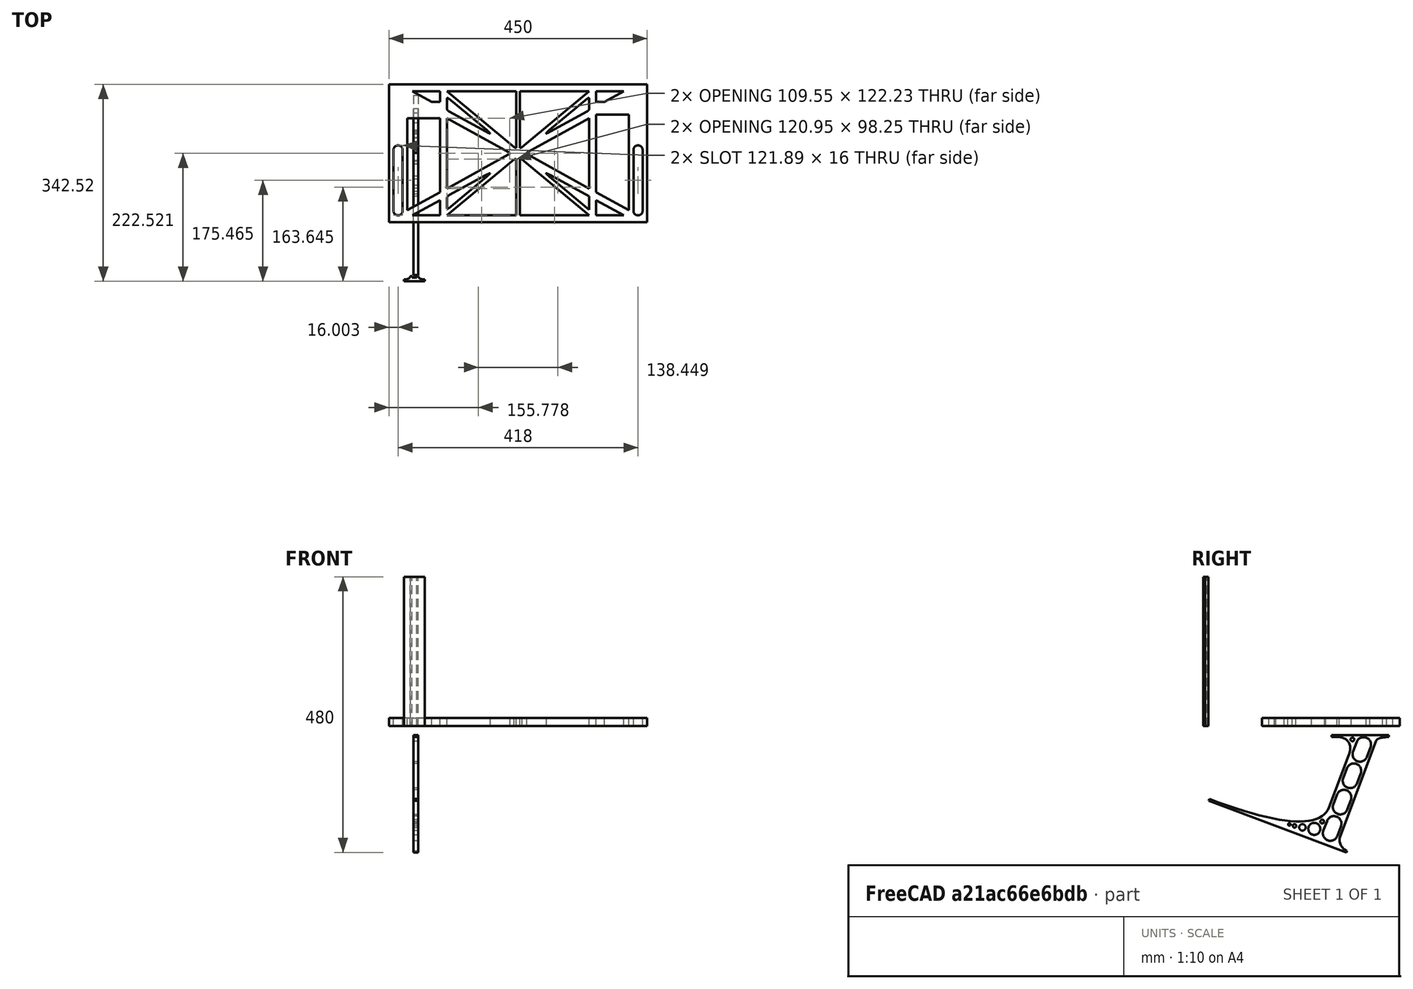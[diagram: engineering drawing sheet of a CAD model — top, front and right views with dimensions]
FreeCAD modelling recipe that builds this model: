
FCSTD DOCUMENT  (FreeCAD 0.19R0.19.2)
Label: laptopStand075
License: All rights reserved
LicenseURL: http://en.wikipedia.org/wiki/All_rights_reserved
objects: Sketcher::SketchObject×3, Part::Extrusion×3
note: 6 computed .brp shape members not serialized (recipe doc carries the construction recipe); baked Part::Feature solids carry a one-line shape summary decoded from their .brp

FEATURE [Sketcher::SketchObject] Sketch
  FullyConstrained = true
  sketch-geometry (160):
    g0: LineSegment StartX=-10.9272 StartY=-82.7794 StartZ=0 EndX=46.0728 EndY=-51.4823 EndZ=0
    g1: LineSegment StartX=366.073 StartY=-91.7794 StartZ=0 EndX=318.073 EndY=-65.424 EndZ=0
    g2: LineSegment StartX=-10.9272 StartY=77.3346 StartZ=0 EndX=-10.9272 EndY=-82.7794 EndZ=0
    g3: LineSegment StartX=375.073 StartY=-82.7794 StartZ=0 EndX=375.073 EndY=83.9235 EndZ=0
    g4: LineSegment StartX=-1.92719 StartY=-91.7794 StartZ=0 EndX=46.0728 EndY=-91.7794 EndZ=0
    g5: LineSegment StartX=318.073 StartY=124.221 StartZ=0 EndX=366.073 EndY=124.221 EndZ=0
    g6: LineSegment StartX=306.073 StartY=124.221 StartZ=0 EndX=189.124 EndY=27.0628 EndZ=0
    g7: LineSegment StartX=58.0728 StartY=-91.7794 StartZ=0 EndX=175.022 EndY=5.37834 EndZ=0
    g8: LineSegment StartX=175.022 StartY=27.0628 StartZ=0 EndX=58.0728 EndY=124.221 EndZ=0
    g9: LineSegment StartX=189.124 StartY=5.37834 StartZ=0 EndX=306.073 EndY=-91.7794 EndZ=0
    g10: LineSegment StartX=306.073 StartY=77.3346 StartZ=0 EndX=306.073 EndY=-44.8935 EndZ=0
    g11: LineSegment StartX=318.073 StartY=83.9235 StartZ=0 EndX=318.073 EndY=-51.4823 EndZ=0
    g12: LineSegment StartX=306.073 StartY=-58.8351 StartZ=0 EndX=306.073 EndY=-81.8102 EndZ=0
    g13: LineSegment StartX=318.073 StartY=-51.4823 StartZ=0 EndX=375.073 EndY=-82.7794 EndZ=0
    g14: LineSegment StartX=318.073 StartY=-65.424 StartZ=0 EndX=318.073 EndY=-91.7794 EndZ=0
    g15: LineSegment StartX=318.073 StartY=-91.7794 StartZ=0 EndX=366.073 EndY=-91.7794 EndZ=0
    g16: LineSegment StartX=58.0728 StartY=-44.8935 StartZ=0 EndX=58.0728 EndY=77.3346 EndZ=0
    g17: LineSegment StartX=46.0728 StartY=-65.424 StartZ=0 EndX=-1.92719 EndY=-91.7794 EndZ=0
    g18: LineSegment StartX=46.0728 StartY=-65.424 StartZ=0 EndX=46.0728 EndY=-91.7794 EndZ=0
    g19: LineSegment StartX=46.0728 StartY=77.3346 StartZ=0 EndX=46.0728 EndY=-51.4823 EndZ=0
    g20: LineSegment StartX=-42.9272 StartY=136.221 StartZ=0 EndX=-42.9272 EndY=-103.779 EndZ=0
    g21: LineSegment StartX=407.073 StartY=136.221 StartZ=0 EndX=407.073 EndY=-103.779 EndZ=0
    g22: LineSegment StartX=179.022 StartY=27.0628 StartZ=0 EndX=179.022 EndY=124.221 EndZ=0
    g23: LineSegment StartX=185.124 StartY=27.0628 StartZ=0 EndX=185.124 EndY=124.221 EndZ=0
    g24: ArcOfCircle CenterX=-26.9272 CenterY=22.1087 CenterZ=0 NormalX=0 NormalY=0 NormalZ=1 AngleXU=0 Radius=8 StartAngle=1e-16 EndAngle=3.14159
    g25: ArcOfCircle CenterX=-26.9272 CenterY=-83.7794 CenterZ=0 NormalX=0 NormalY=0 NormalZ=1 AngleXU=0 Radius=8 StartAngle=3.14159 EndAngle=6.28319
    g26: LineSegment StartX=-34.9272 StartY=22.1087 StartZ=0 EndX=-34.9272 EndY=-83.7794 EndZ=0
    g27: LineSegment StartX=-18.9272 StartY=22.1087 StartZ=0 EndX=-18.9272 EndY=-83.7794 EndZ=0
    g28: LineSegment StartX=185.124 StartY=-91.7794 StartZ=0 EndX=306.073 EndY=-91.7794 EndZ=0
    g29: LineSegment StartX=179.022 StartY=-91.7794 StartZ=0 EndX=58.0728 EndY=-91.7794 EndZ=0
    g30: LineSegment StartX=306.073 StartY=124.221 StartZ=0 EndX=185.124 EndY=124.221 EndZ=0
    g31: LineSegment StartX=179.022 StartY=124.221 StartZ=0 EndX=58.0728 EndY=124.221 EndZ=0
    g32: ArcOfCircle CenterX=391.073 CenterY=22.1087 CenterZ=0 NormalX=0 NormalY=0 NormalZ=1 AngleXU=0 Radius=8 StartAngle=-4.4e-15 EndAngle=3.14159
    g33: LineSegment StartX=399.073 StartY=22.1087 StartZ=0 EndX=399.073 EndY=-83.7794 EndZ=0
    g34: LineSegment StartX=383.073 StartY=22.1087 StartZ=0 EndX=383.073 EndY=-83.7794 EndZ=0
    g35: ArcOfCircle CenterX=391.073 CenterY=-83.7794 CenterZ=0 NormalX=0 NormalY=0 NormalZ=1 AngleXU=0 Radius=8 StartAngle=3.14159 EndAngle=6.28319
    g36: Circle CenterX=175.022 CenterY=27.0628 CenterZ=0 NormalX=0 NormalY=0 NormalZ=1 AngleXU=0 Radius=1
    g37: Circle CenterX=179.022 CenterY=24.8665 CenterZ=0 NormalX=0 NormalY=0 NormalZ=1 AngleXU=0 Radius=1
    g38: Circle CenterX=179.022 CenterY=27.0628 CenterZ=0 NormalX=0 NormalY=0 NormalZ=1 AngleXU=0 Radius=1
    g39: BSplineCurve PolesCount=3 KnotsCount=2 Degree=2 IsPeriodic=0
    g40: GeomPoint X=175.022 Y=27.0628 Z=0
    g41: GeomPoint X=179.022 Y=27.0628 Z=0
    g42: Circle CenterX=189.124 CenterY=27.0628 CenterZ=0 NormalX=0 NormalY=0 NormalZ=1 AngleXU=0 Radius=1
    g43: Circle CenterX=185.124 CenterY=24.8665 CenterZ=0 NormalX=0 NormalY=0 NormalZ=1 AngleXU=0 Radius=1
    g44: Circle CenterX=185.124 CenterY=27.0628 CenterZ=0 NormalX=0 NormalY=0 NormalZ=1 AngleXU=0 Radius=1
    g45: BSplineCurve PolesCount=3 KnotsCount=2 Degree=2 IsPeriodic=0
    g46: GeomPoint X=189.124 Y=27.0628 Z=0
    g47: GeomPoint X=185.124 Y=27.0628 Z=0
    g48: Circle CenterX=175.022 CenterY=5.37834 CenterZ=0 NormalX=0 NormalY=0 NormalZ=1 AngleXU=0 Radius=1
    g49: Circle CenterX=179.022 CenterY=7.57463 CenterZ=0 NormalX=0 NormalY=0 NormalZ=1 AngleXU=0 Radius=1
    g50: Circle CenterX=179.022 CenterY=5.34704 CenterZ=0 NormalX=0 NormalY=0 NormalZ=1 AngleXU=0 Radius=1
    g51: BSplineCurve PolesCount=3 KnotsCount=2 Degree=2 IsPeriodic=0
    g52: GeomPoint X=175.022 Y=5.37834 Z=0
    g53: GeomPoint X=179.022 Y=5.34704 Z=0
    g54: Circle CenterX=189.124 CenterY=5.37834 CenterZ=0 NormalX=0 NormalY=0 NormalZ=1 AngleXU=0 Radius=1
    g55: Circle CenterX=185.124 CenterY=7.57463 CenterZ=0 NormalX=0 NormalY=0 NormalZ=1 AngleXU=0 Radius=1
    g56: Circle CenterX=185.124 CenterY=5.34704 CenterZ=0 NormalX=0 NormalY=0 NormalZ=1 AngleXU=0 Radius=1
    g57: BSplineCurve PolesCount=3 KnotsCount=2 Degree=2 IsPeriodic=0
    g58: GeomPoint X=189.124 Y=5.37834 Z=0
    g59: GeomPoint X=185.124 Y=5.34704 Z=0
    g60: LineSegment StartX=179.022 StartY=5.34704 StartZ=0 EndX=179.022 EndY=-91.7794 EndZ=0
    g61: LineSegment StartX=185.124 StartY=-91.7794 StartZ=0 EndX=185.124 EndY=5.34704 EndZ=0
    g62: Circle CenterX=165.871 CenterY=18.1458 CenterZ=0 NormalX=0 NormalY=0 NormalZ=1 AngleXU=0 Radius=1
    g63: Circle CenterX=169.377 CenterY=16.2206 CenterZ=0 NormalX=0 NormalY=0 NormalZ=1 AngleXU=0 Radius=1
    g64: Circle CenterX=165.871 CenterY=14.2954 CenterZ=0 NormalX=0 NormalY=0 NormalZ=1 AngleXU=0 Radius=1
    g65: BSplineCurve PolesCount=3 KnotsCount=2 Degree=2 IsPeriodic=0
    g66: GeomPoint X=165.871 Y=18.1458 Z=0
    g67: GeomPoint X=165.871 Y=14.2954 Z=0
    g68: Circle CenterX=198.275 CenterY=18.1458 CenterZ=0 NormalX=0 NormalY=0 NormalZ=1 AngleXU=0 Radius=1
    g69: Circle CenterX=194.768 CenterY=16.2206 CenterZ=0 NormalX=0 NormalY=0 NormalZ=1 AngleXU=0 Radius=1
    g70: Circle CenterX=198.275 CenterY=14.2954 CenterZ=0 NormalX=0 NormalY=0 NormalZ=1 AngleXU=0 Radius=1
    g71: BSplineCurve PolesCount=3 KnotsCount=2 Degree=2 IsPeriodic=0
    g72: GeomPoint X=198.275 Y=18.1458 Z=0
    g73: GeomPoint X=198.275 Y=14.2954 Z=0
    g74: LineSegment StartX=165.871 StartY=18.1458 StartZ=0 EndX=58.0728 EndY=77.3346 EndZ=0
    g75: LineSegment StartX=58.0728 StartY=-44.8935 StartZ=0 EndX=165.871 EndY=14.2954 EndZ=0
    g76: LineSegment StartX=198.275 StartY=18.1458 StartZ=0 EndX=306.073 EndY=77.3346 EndZ=0
    g77: LineSegment StartX=198.275 StartY=14.2954 StartZ=0 EndX=306.073 EndY=-44.8935 EndZ=0
    g78: LineSegment StartX=407.073 StartY=-103.779 StartZ=0 EndX=-42.9272 EndY=-103.779 EndZ=0
    g79: LineSegment StartX=407.073 StartY=136.221 StartZ=0 EndX=-42.9272 EndY=136.221 EndZ=0
    g80: LineSegment StartX=46.0728 StartY=77.3346 StartZ=0 EndX=-10.9272 EndY=77.3346 EndZ=0
    g81: LineSegment StartX=46.0728 StartY=105.865 StartZ=0 EndX=31.5028 EndY=105.865 EndZ=0
    g82: LineSegment StartX=46.0728 StartY=124.221 StartZ=0 EndX=46.0728 EndY=105.865 EndZ=0
    g83: LineSegment StartX=-1.92719 StartY=124.221 StartZ=0 EndX=31.5028 EndY=105.865 EndZ=0
    g84: LineSegment StartX=46.0728 StartY=124.221 StartZ=0 EndX=-1.92719 EndY=124.221 EndZ=0
    g85: LineSegment StartX=318.073 StartY=83.9235 StartZ=0 EndX=375.073 EndY=83.9235 EndZ=0
    g86: LineSegment StartX=318.073 StartY=105.865 StartZ=0 EndX=332.643 EndY=105.865 EndZ=0
    g87: LineSegment StartX=332.643 StartY=105.865 StartZ=0 EndX=366.073 EndY=124.221 EndZ=0
    g88: LineSegment StartX=318.073 StartY=124.221 StartZ=0 EndX=318.073 EndY=105.865 EndZ=0
    g89: Circle CenterX=125.607 CenterY=54.1951 CenterZ=0 NormalX=0 NormalY=0 NormalZ=1 AngleXU=0 Radius=1
    g90: Circle CenterX=139.632 CenterY=46.4944 CenterZ=0 NormalX=0 NormalY=0 NormalZ=1 AngleXU=0 Radius=1
    g91: Circle CenterX=127.326 CenterY=56.7187 CenterZ=0 NormalX=0 NormalY=0 NormalZ=1 AngleXU=0 Radius=1
    g92: BSplineCurve PolesCount=3 KnotsCount=2 Degree=2 IsPeriodic=0
    g93: GeomPoint X=125.607 Y=54.1951 Z=0
    g94: GeomPoint X=127.326 Y=56.7187 Z=0
    g95: Circle CenterX=236.821 CenterY=56.7187 CenterZ=0 NormalX=0 NormalY=0 NormalZ=1 AngleXU=0 Radius=1
    g96: Circle CenterX=224.513 CenterY=46.4944 CenterZ=0 NormalX=0 NormalY=0 NormalZ=1 AngleXU=0 Radius=1
    g97: Circle CenterX=238.538 CenterY=54.1951 CenterZ=0 NormalX=0 NormalY=0 NormalZ=1 AngleXU=0 Radius=1
    g98: BSplineCurve PolesCount=3 KnotsCount=2 Degree=2 IsPeriodic=0
    g99: GeomPoint X=236.821 Y=56.7187 Z=0
    g100: GeomPoint X=238.538 Y=54.1951 Z=0
    g101: Circle CenterX=238.538 CenterY=-21.7539 CenterZ=0 NormalX=0 NormalY=0 NormalZ=1 AngleXU=0 Radius=1
    g102: Circle CenterX=224.513 CenterY=-14.0532 CenterZ=0 NormalX=0 NormalY=0 NormalZ=1 AngleXU=0 Radius=1
    g103: Circle CenterX=236.821 CenterY=-24.2775 CenterZ=0 NormalX=0 NormalY=0 NormalZ=1 AngleXU=0 Radius=1
    g104: BSplineCurve PolesCount=3 KnotsCount=2 Degree=2 IsPeriodic=0
    g105: GeomPoint X=238.538 Y=-21.7539 Z=0
    g106: GeomPoint X=236.821 Y=-24.2775 Z=0
    g107: LineSegment StartX=238.538 StartY=-21.7539 StartZ=0 EndX=306.073 EndY=-58.8351 EndZ=0
    g108: LineSegment StartX=236.821 StartY=-24.2775 StartZ=0 EndX=306.073 EndY=-81.8102 EndZ=0
    g109: Circle CenterX=125.607 CenterY=-21.7539 CenterZ=0 NormalX=0 NormalY=0 NormalZ=1 AngleXU=0 Radius=1
    g110: Circle CenterX=139.632 CenterY=-14.0532 CenterZ=0 NormalX=0 NormalY=0 NormalZ=1 AngleXU=0 Radius=1
    g111: Circle CenterX=127.325 CenterY=-24.2775 CenterZ=0 NormalX=0 NormalY=0 NormalZ=1 AngleXU=0 Radius=1
    g112: BSplineCurve PolesCount=3 KnotsCount=2 Degree=2 IsPeriodic=0
    g113: GeomPoint X=125.607 Y=-21.7539 Z=0
    g114: GeomPoint X=127.325 Y=-24.2775 Z=0
    g115: Circle CenterX=302.996 CenterY=111.695 CenterZ=0 NormalX=0 NormalY=0 NormalZ=1 AngleXU=0 Radius=1
    g116: Circle CenterX=306.073 CenterY=114.251 CenterZ=0 NormalX=0 NormalY=0 NormalZ=1 AngleXU=0 Radius=1
    g117: Circle CenterX=306.073 CenterY=110.251 CenterZ=0 NormalX=0 NormalY=0 NormalZ=1 AngleXU=0 Radius=1
    g118: BSplineCurve PolesCount=3 KnotsCount=2 Degree=2 IsPeriodic=0
    g119: GeomPoint X=302.996 Y=111.695 Z=0
    g120: GeomPoint X=306.073 Y=110.251 Z=0
    g121: Circle CenterX=306.073 CenterY=95.2763 CenterZ=0 NormalX=0 NormalY=0 NormalZ=1 AngleXU=0 Radius=1
    g122: Circle CenterX=306.073 CenterY=91.2763 CenterZ=0 NormalX=0 NormalY=0 NormalZ=1 AngleXU=0 Radius=1
    g123: Circle CenterX=302.567 CenterY=89.3511 CenterZ=0 NormalX=0 NormalY=0 NormalZ=1 AngleXU=0 Radius=1
    g124: BSplineCurve PolesCount=3 KnotsCount=2 Degree=2 IsPeriodic=0
    g125: GeomPoint X=306.073 Y=95.2763 Z=0
    g126: GeomPoint X=302.567 Y=89.3511 Z=0
    g127: LineSegment StartX=306.073 StartY=110.251 StartZ=0 EndX=306.073 EndY=95.2763 EndZ=0
    g128: LineSegment StartX=302.996 StartY=111.695 StartZ=0 EndX=236.821 EndY=56.7187 EndZ=0
    g129: LineSegment StartX=238.538 StartY=54.1951 StartZ=0 EndX=302.567 EndY=89.3511 EndZ=0
    g130: Circle CenterX=61.1496 CenterY=111.695 CenterZ=0 NormalX=0 NormalY=0 NormalZ=1 AngleXU=0 Radius=1
    g131: Circle CenterX=58.0728 CenterY=114.251 CenterZ=0 NormalX=0 NormalY=0 NormalZ=1 AngleXU=0 Radius=1
    g132: Circle CenterX=58.0728 CenterY=110.251 CenterZ=0 NormalX=0 NormalY=0 NormalZ=1 AngleXU=0 Radius=1
    g133: BSplineCurve PolesCount=3 KnotsCount=2 Degree=2 IsPeriodic=0
    g134: GeomPoint X=61.1496 Y=111.695 Z=0
    g135: GeomPoint X=58.0728 Y=110.251 Z=0
    g136: Circle CenterX=61.5791 CenterY=89.3511 CenterZ=0 NormalX=0 NormalY=0 NormalZ=1 AngleXU=0 Radius=1
    g137: Circle CenterX=58.0728 CenterY=91.2763 CenterZ=0 NormalX=0 NormalY=0 NormalZ=1 AngleXU=0 Radius=1
    g138: Circle CenterX=58.0728 CenterY=95.2763 CenterZ=0 NormalX=0 NormalY=0 NormalZ=1 AngleXU=0 Radius=1
    g139: BSplineCurve PolesCount=3 KnotsCount=2 Degree=2 IsPeriodic=0
    g140: GeomPoint X=61.5791 Y=89.3511 Z=0
    g141: GeomPoint X=58.0728 Y=95.2763 Z=0
    g142: LineSegment StartX=58.0728 StartY=110.251 StartZ=0 EndX=58.0728 EndY=95.2763 EndZ=0
    g143: LineSegment StartX=61.1496 StartY=111.695 StartZ=0 EndX=127.326 EndY=56.7187 EndZ=0
    g144: LineSegment StartX=125.607 StartY=54.1951 StartZ=0 EndX=61.5791 EndY=89.3511 EndZ=0
    g145: Circle CenterX=61.5791 CenterY=-56.9099 CenterZ=0 NormalX=0 NormalY=0 NormalZ=1 AngleXU=0 Radius=1
    g146: Circle CenterX=58.0728 CenterY=-58.8351 CenterZ=0 NormalX=0 NormalY=0 NormalZ=1 AngleXU=0 Radius=1
    g147: Circle CenterX=58.0728 CenterY=-62.8351 CenterZ=0 NormalX=0 NormalY=0 NormalZ=1 AngleXU=0 Radius=1
    g148: BSplineCurve PolesCount=3 KnotsCount=2 Degree=2 IsPeriodic=0
    g149: GeomPoint X=61.5791 Y=-56.9099 Z=0
    g150: GeomPoint X=58.0728 Y=-62.8351 Z=0
    g151: Circle CenterX=58.0728 CenterY=-77.8102 CenterZ=0 NormalX=0 NormalY=0 NormalZ=1 AngleXU=0 Radius=1
    g152: Circle CenterX=58.0728 CenterY=-81.8102 CenterZ=0 NormalX=0 NormalY=0 NormalZ=1 AngleXU=0 Radius=1
    g153: Circle CenterX=61.1496 CenterY=-79.2541 CenterZ=0 NormalX=0 NormalY=0 NormalZ=1 AngleXU=0 Radius=1
    g154: BSplineCurve PolesCount=3 KnotsCount=2 Degree=2 IsPeriodic=0
    g155: GeomPoint X=58.0728 Y=-77.8102 Z=0
    g156: GeomPoint X=61.1496 Y=-79.2541 Z=0
    g157: LineSegment StartX=58.0728 StartY=-62.8351 StartZ=0 EndX=58.0728 EndY=-77.8102 EndZ=0
    g158: LineSegment StartX=61.1496 StartY=-79.2541 StartZ=0 EndX=127.325 EndY=-24.2775 EndZ=0
    g159: LineSegment StartX=125.607 StartY=-21.7539 StartZ=0 EndX=61.5791 EndY=-56.9099 EndZ=0
  constraints (281):
    c: Horizontal(g4)
    c: Horizontal(g5)
    c: Tangent(g10,g12)
    c: Coincident(g11,g13)
    c: Coincident(g14,g1)
    c: Tangent(g11,g14)
    c: Coincident(g18,g17)
    c: Coincident(g0,g19)
    c: Block(g8)
    c: Block(g6)
    c: Block(g13)
    c: Block(g3)
    c: Block(g12)
    c: Block(g1)
    c: Block(g14)
    c: Block(g9)
    c: Block(g7)
    c: Block(g18)
    c: Block(g17)
    c: Block(g0)
    c: Block(g2)
    c: Block(g10)
    c: Block(g5)
    c: Block(g15)
    c: Block(g4)
    c: Vertical(g20)
    c: Vertical(g21)
    c: Block(g21)
    c: Block(g20)
    c: Vertical(g22)
    c: Vertical(g23)
    c: Block(g22)
    c: Block(g23)
    c: Tangent(g24,g27) = 1.5708
    c: Tangent(g24,g26) = -1.5708
    c: Tangent(g26,g25) = -1.5708
    c: Tangent(g27,g25) = 1.5708
    c: Vertical(g26)
    c: Equal(g24,g25)
    c: Block(g27)
    c: Block(g26)
    c: Coincident(g28,g9)
    c: Horizontal(g28)
    c: Coincident(g29,g7)
    c: Horizontal(g29)
    c: Coincident(g30,g6)
    c: Coincident(g30,g23)
    c: Horizontal(g30)
    c: Coincident(g31,g22)
    c: Coincident(g31,g8)
    c: Horizontal(g31)
    c: Tangent(g32,g33) = 1.5708
    c: Tangent(g33,g35) = 1.5708
    c: Equal(g32,g35)
    c: Coincident(g34,g32)
    c: Coincident(g34,g35)
    c: Block(g33)
    c: Block(g34)
    c: Coincident(g39,g8)
    c: Weight(g36) = 1
    c: Equal(g36,g37)
    c: Equal(g36,g38)
    c: Coincident(g39,g22)
    c: InternalAlignment(g36,g39)
    c: InternalAlignment(g37,g39)
    c: InternalAlignment(g38,g39)
    c: InternalAlignment(g40,g39)
    c: InternalAlignment(g41,g39)
    c: Coincident(g45,g6)
    c: Weight(g42) = 1
    c: Equal(g42,g43)
    c: Equal(g42,g44)
    c: Coincident(g45,g23)
    c: InternalAlignment(g42,g45)
    c: InternalAlignment(g43,g45)
    c: InternalAlignment(g44,g45)
    c: InternalAlignment(g46,g45)
    c: InternalAlignment(g47,g45)
    c: Block(g45)
    c: Block(g39)
    c: Coincident(g51,g7)
    c: Weight(g48) = 1
    c: Equal(g48,g49)
    c: Equal(g48,g50)
    c: InternalAlignment(g48,g51)
    c: InternalAlignment(g49,g51)
    c: InternalAlignment(g50,g51)
    c: InternalAlignment(g52,g51)
    c: InternalAlignment(g53,g51)
    c: Weight(g54) = 1
    c: Equal(g54,g55)
    c: Equal(g54,g56)
    c: InternalAlignment(g54,g57)
    c: InternalAlignment(g55,g57)
    c: InternalAlignment(g56,g57)
    c: InternalAlignment(g58,g57)
    c: InternalAlignment(g59,g57)
    c: Block(g57)
    c: Block(g51)
    c: Coincident(g60,g51)
    c: Coincident(g60,g29)
    c: Vertical(g60)
    c: Coincident(g61,g28)
    c: Coincident(g61,g57)
    c: Vertical(g61)
    c: Weight(g62) = 1
    c: Equal(g62,g63)
    c: Equal(g62,g64)
    c: InternalAlignment(g62,g65)
    c: InternalAlignment(g63,g65)
    c: InternalAlignment(g64,g65)
    c: InternalAlignment(g66,g65)
    c: InternalAlignment(g67,g65)
    c: Weight(g68) = 1
    c: Equal(g68,g69)
    c: Equal(g68,g70)
    c: InternalAlignment(g68,g71)
    c: InternalAlignment(g69,g71)
    c: InternalAlignment(g70,g71)
    c: InternalAlignment(g72,g71)
    c: InternalAlignment(g73,g71)
    c: Block(g65)
    c: Block(g71)
    c: Coincident(g74,g65)
    c: Coincident(g74,g16)
    c: Coincident(g75,g16)
    c: Coincident(g75,g65)
    c: Coincident(g76,g71)
    c: Coincident(g76,g10)
    c: Coincident(g77,g71)
    c: Coincident(g77,g10)
    c: Block(g16)
    c: Coincident(g78,g21)
    c: Coincident(g78,g20)
    c: Horizontal(g78)
    c: Distance(g78) = 450
    c: Coincident(g79,g21)
    c: Coincident(g79,g20)
    c: Horizontal(g79)
    c: Horizontal(g80)
    c: Coincident(g19,g80)
    c: Horizontal(g81)
    c: Vertical(g82)
    c: Block(g82)
    c: Block(g81)
    c: Block(g80)
    c: Distance(g82) = 18.3554
    c: Coincident(g84,g82)
    c: Coincident(g84,g83)
    c: Horizontal(g84)
    c: Block(g84)
    c: Block(g83)
    c: Coincident(g81,g83)
    c: Coincident(g2,g80)
    c: Coincident(g85,g11)
    c: Horizontal(g85)
    c: Horizontal(g86)
    c: Block(g85)
    c: Coincident(g87,g5)
    c: Coincident(g88,g5)
    c: Coincident(g88,g86)
    c: Vertical(g88)
    c: Block(g88)
    c: Coincident(g86,g87)
    c: Block(g87)
    c: Coincident(g3,g85)
    c: Weight(g89) = 1
    c: Equal(g89,g90)
    c: Equal(g89,g91)
    c: InternalAlignment(g89,g92)
    c: InternalAlignment(g90,g92)
    c: InternalAlignment(g91,g92)
    c: InternalAlignment(g93,g92)
    c: InternalAlignment(g94,g92)
    c: Block(g92)
    c: Weight(g95) = 1
    c: Equal(g95,g96)
    c: Equal(g95,g97)
    c: InternalAlignment(g95,g98)
    c: InternalAlignment(g96,g98)
    c: InternalAlignment(g97,g98)
    c: InternalAlignment(g99,g98)
    c: InternalAlignment(g100,g98)
    c: Block(g98)
    c: Weight(g101) = 1
    c: Equal(g101,g102)
    c: Equal(g101,g103)
    c: InternalAlignment(g101,g104)
    c: InternalAlignment(g102,g104)
    c: InternalAlignment(g103,g104)
    c: InternalAlignment(g105,g104)
    c: InternalAlignment(g106,g104)
    c: Block(g104)
    c: Coincident(g107,g104)
    c: Coincident(g107,g12)
    c: Coincident(g108,g104)
    c: Coincident(g108,g12)
    c: Weight(g109) = 1
    c: Equal(g109,g110)
    c: Equal(g109,g111)
    c: InternalAlignment(g109,g112)
    c: InternalAlignment(g110,g112)
    c: InternalAlignment(g111,g112)
    c: InternalAlignment(g113,g112)
    c: InternalAlignment(g114,g112)
    c: Block(g112)
    c: Weight(g115) = 1
    c: Equal(g115,g116)
    c: Equal(g115,g117)
    c: InternalAlignment(g115,g118)
    c: InternalAlignment(g116,g118)
    c: InternalAlignment(g117,g118)
    c: InternalAlignment(g119,g118)
    c: InternalAlignment(g120,g118)
    c: Weight(g121) = 1
    c: Equal(g121,g122)
    c: Equal(g121,g123)
    c: InternalAlignment(g121,g124)
    c: InternalAlignment(g122,g124)
    c: InternalAlignment(g123,g124)
    c: InternalAlignment(g125,g124)
    c: InternalAlignment(g126,g124)
    c: Block(g118)
    c: Block(g124)
    c: Coincident(g127,g118)
    c: Coincident(g127,g124)
    c: Vertical(g127)
    c: Coincident(g128,g118)
    c: Coincident(g128,g98)
    c: Coincident(g129,g98)
    c: Coincident(g129,g124)
    c: Weight(g130) = 1
    c: Equal(g130,g131)
    c: Equal(g130,g132)
    c: InternalAlignment(g130,g133)
    c: InternalAlignment(g131,g133)
    c: InternalAlignment(g132,g133)
    c: InternalAlignment(g134,g133)
    c: InternalAlignment(g135,g133)
    c: Weight(g136) = 1
    c: Equal(g136,g137)
    c: Equal(g136,g138)
    c: InternalAlignment(g136,g139)
    c: InternalAlignment(g137,g139)
    c: InternalAlignment(g138,g139)
    c: InternalAlignment(g140,g139)
    c: InternalAlignment(g141,g139)
    c: Block(g133)
    c: Block(g139)
    c: Coincident(g142,g133)
    c: Coincident(g142,g139)
    c: Vertical(g142)
    c: Coincident(g143,g133)
    c: Coincident(g143,g92)
    c: Coincident(g144,g92)
    c: Coincident(g144,g139)
    c: Weight(g145) = 1
    c: Equal(g145,g146)
    c: Equal(g145,g147)
    c: InternalAlignment(g145,g148)
    c: InternalAlignment(g146,g148)
    c: InternalAlignment(g147,g148)
    c: InternalAlignment(g149,g148)
    c: InternalAlignment(g150,g148)
    c: Weight(g151) = 1
    c: Equal(g151,g152)
    c: Equal(g151,g153)
    c: InternalAlignment(g151,g154)
    c: InternalAlignment(g152,g154)
    c: InternalAlignment(g153,g154)
    c: InternalAlignment(g155,g154)
    c: InternalAlignment(g156,g154)
    c: Block(g148)
    c: Block(g154)
    c: Coincident(g157,g148)
    c: Coincident(g157,g154)
    c: Vertical(g157)
    c: Coincident(g158,g154)
    c: Coincident(g158,g112)
    c: Coincident(g159,g112)
    c: Coincident(g159,g148)
FEATURE [Sketcher::SketchObject] Sketch001
  FullyConstrained = true
  MapMode = 4
  Placement = pos=(0,0,0) rot=(0.57735,0.57735,0.57735;2.0944rad)
  Support = -> [Sketch]
  sketch-geometry (46):
    g0: BSplineCurve PolesCount=3 KnotsCount=2 Degree=2 IsPeriodic=0
    g1: ArcOfCircle CenterX=73.1223 CenterY=-32.291 CenterZ=0 NormalX=0 NormalY=0 NormalZ=1 AngleXU=0 Radius=13 StartAngle=5.92268 EndAngle=9.06428
    g2: ArcOfCircle CenterX=66.7816 CenterY=-49.1439 CenterZ=0 NormalX=0 NormalY=0 NormalZ=1 AngleXU=0 Radius=13 StartAngle=2.78068 EndAngle=5.92131
    g3: ArcOfCircle CenterX=55.9263 CenterY=-78.1807 CenterZ=0 NormalX=0 NormalY=0 NormalZ=1 AngleXU=0 Radius=13 StartAngle=5.92268 EndAngle=9.06428
    g4: ArcOfCircle CenterX=49.5884 CenterY=-95.0342 CenterZ=0 NormalX=0 NormalY=0 NormalZ=1 AngleXU=0 Radius=13 StartAngle=2.78068 EndAngle=5.92131
    g5: ArcOfCircle CenterX=38.7206 CenterY=-124.067 CenterZ=0 NormalX=0 NormalY=0 NormalZ=1 AngleXU=0 Radius=13 StartAngle=5.92268 EndAngle=9.06428
    g6: ArcOfCircle CenterX=32.3875 CenterY=-140.92 CenterZ=0 NormalX=0 NormalY=0 NormalZ=1 AngleXU=0 Radius=13 StartAngle=2.78068 EndAngle=5.92131
    g7: ArcOfCircle CenterX=21.4715 CenterY=-169.934 CenterZ=0 NormalX=0 NormalY=0 NormalZ=1 AngleXU=0 Radius=13 StartAngle=5.92268 EndAngle=9.06428
    g8: ArcOfCircle CenterX=15.1336 CenterY=-186.787 CenterZ=0 NormalX=0 NormalY=0 NormalZ=1 AngleXU=0 Radius=13 StartAngle=2.78068 EndAngle=5.92131
    g9-g12: Circle x4 (B-spline internal-alignment scaffolding for g13; pole/knot coordinates omitted)
    g13: BSplineCurve PolesCount=4 KnotsCount=2 Degree=3 IsPeriodic=0
    g14: GeomPoint X=28.8094 Y=-19.0875 Z=0
    g15: GeomPoint X=47.0443 Y=-50.4712 Z=0
    g16: Circle CenterX=53.5586 CenterY=-23.2695 CenterZ=0 NormalX=0 NormalY=0 NormalZ=1 AngleXU=0 Radius=3.24518
    g17: Circle CenterX=-195.441 CenterY=-127.082 CenterZ=0 NormalX=0 NormalY=0 NormalZ=1 AngleXU=0 Radius=1
    g18: Circle CenterX=-8.24091 CenterY=-197.481 CenterZ=0 NormalX=0 NormalY=0 NormalZ=1 AngleXU=0 Radius=1
    g19: Circle CenterX=12.8789 CenterY=-141.321 CenterZ=0 NormalX=0 NormalY=0 NormalZ=1 AngleXU=0 Radius=1
    g20: BSplineCurve PolesCount=3 KnotsCount=2 Degree=2 IsPeriodic=0
    g21: GeomPoint X=-195.441 Y=-127.082 Z=0
    g22: GeomPoint X=12.8789 Y=-141.321 Z=0
    g23: Circle CenterX=-12.8016 CenterY=-179.036 CenterZ=0 NormalX=0 NormalY=0 NormalZ=1 AngleXU=0 Radius=10.5072
    g24: Circle CenterX=0.933922 CenterY=-166.43 CenterZ=0 NormalX=0 NormalY=0 NormalZ=1 AngleXU=0 Radius=3.26661
    g25: Circle CenterX=-33.5518 CenterY=-176.44 CenterZ=0 NormalX=0 NormalY=0 NormalZ=1 AngleXU=0 Radius=5.64388
    g26: Circle CenterX=-47.2366 CenterY=-173.859 CenterZ=0 NormalX=0 NormalY=0 NormalZ=1 AngleXU=0 Radius=3.01653
    g27: Circle CenterX=-56.2595 CenterY=-171.456 CenterZ=0 NormalX=0 NormalY=0 NormalZ=1 AngleXU=0 Radius=2.12826
    g28: ArcOfCircle CenterX=51.2151 CenterY=-198.473 CenterZ=0 NormalX=0 NormalY=0 NormalZ=1 AngleXU=0 Radius=20 StartAngle=2.78189 EndAngle=4.35269
    g29: LineSegment StartX=32.4951 StartY=-191.433 StartZ=0 EndX=94.6578 EndY=-26.1352 EndZ=0
    g30: LineSegment StartX=43.1192 StartY=-220.001 StartZ=0 EndX=-196.497 EndY=-129.89 EndZ=0
    g31: LineSegment StartX=43.1192 StartY=-220.001 StartZ=0 EndX=44.1752 EndY=-217.193 EndZ=0
    g32: LineSegment StartX=117.223 StartY=-19.0875 StartZ=0 EndX=117.223 EndY=-16.0875 EndZ=0
    g33: LineSegment StartX=117.223 StartY=-16.0875 StartZ=0 EndX=17.2232 EndY=-16.0875 EndZ=0
    g34: LineSegment StartX=17.2232 StartY=-16.0875 StartZ=0 EndX=17.2232 EndY=-19.0875 EndZ=0
    g35: LineSegment StartX=28.8094 StartY=-19.0875 StartZ=0 EndX=17.2232 EndY=-19.0875 EndZ=0
    g36: LineSegment StartX=47.0443 StartY=-50.4712 StartZ=0 EndX=12.8789 EndY=-141.321 EndZ=0
    g37: LineSegment StartX=-195.441 StartY=-127.082 StartZ=0 EndX=-196.497 EndY=-129.89 EndZ=0
    g38: LineSegment StartX=85.2866 StartY=-36.8766 StartZ=0 EndX=78.9396 EndY=-53.7463 EndZ=0
    g39: LineSegment StartX=60.9579 StartY=-27.7053 StartZ=0 EndX=54.6191 EndY=-44.5532 EndZ=0
    g40: LineSegment StartX=68.0907 StartY=-82.7664 StartZ=0 EndX=61.7465 EndY=-99.6365 EndZ=0
    g41: LineSegment StartX=43.7619 StartY=-73.595 StartZ=0 EndX=37.426 EndY=-90.4435 EndZ=0
    g42: LineSegment StartX=50.885 StartY=-128.652 StartZ=0 EndX=44.5456 EndY=-145.522 EndZ=0
    g43: LineSegment StartX=26.5562 StartY=-119.481 StartZ=0 EndX=20.2251 EndY=-136.329 EndZ=0
    g44: LineSegment StartX=9.3071 StartY=-165.349 StartZ=0 EndX=2.97115 EndY=-182.197 EndZ=0
    g45: LineSegment StartX=33.6358 StartY=-174.52 StartZ=0 EndX=27.2917 EndY=-191.39 EndZ=0
  constraints (71):
    c: Block(g0)
    c: Block(g1)
    c: Block(g2)
    c: Block(g4)
    c: Block(g3)
    c: Block(g6)
    c: Block(g5)
    c: Block(g8)
    c: Block(g7)
    c: Weight(g9) = 1
    c: Equal(g9,g10)
    c: Equal(g9,g11)
    c: Equal(g9,g12)
    c: InternalAlignment(g9-g12 -> g13) x4
    c: InternalAlignment(g14,g13)
    c: InternalAlignment(g15,g13)
    c: Block(g16)
    c: Weight(g17) = 1
    c: Equal(g17,g18)
    c: Equal(g17,g19)
    c: InternalAlignment(g17,g20)
    c: InternalAlignment(g18,g20)
    c: InternalAlignment(g19,g20)
    c: InternalAlignment(g21,g20)
    c: InternalAlignment(g22,g20)
    c: Block(g20)
    c: Block(g23)
    c: Block(g24)
    c: Block(g25)
    c: Block(g26)
    c: Block(g27)
    c: Block(g28)
    c: Coincident(g29,g28)
    c: Coincident(g29,g0)
    c: Block(g13)
    c: Coincident(g31,g30)
    c: Coincident(g31,g28)
    c: Block(g31)
    c: Coincident(g32,g0)
    c: Vertical(g32)
    c: Coincident(g33,g32)
    c: Horizontal(g33)
    c: Coincident(g34,g33)
    c: Vertical(g34)
    c: Block(g33)
    c: Coincident(g35,g13)
    c: Coincident(g35,g34)
    c: Horizontal(g35)
    c: Coincident(g36,g13)
    c: Coincident(g36,g20)
    c: Coincident(g37,g20)
    c: Coincident(g37,g30)
    c: Block(g30)
    c: Coincident(g38,g1)
    c: Coincident(g38,g2)
    c: Coincident(g39,g1)
    c: Coincident(g39,g2)
    c: Coincident(g40,g3)
    c: Coincident(g40,g4)
    c: Coincident(g41,g3)
    c: Coincident(g41,g4)
    c: Coincident(g42,g5)
    c: Coincident(g42,g6)
    c: Coincident(g43,g5)
    c: Coincident(g43,g6)
    c: Coincident(g44,g7)
    c: Coincident(g44,g8)
    c: Coincident(g45,g7)
    c: Coincident(g45,g8)
    c: Distance(g30) = 256
    c: Distance(g33) = 100
FEATURE [Part::Extrusion] Extrude002
  Base = -> Sketch001
  Dir = (1,0,0)
  DirMode = 2
  FaceMakerClass = Part::FaceMakerBullseye
  LengthFwd = 8
  LengthRev = 0
  Solid = true
  Symmetric = false
FEATURE [Sketcher::SketchObject] Sketch002
  FullyConstrained = true
  sketch-geometry (20):
    g0: LineSegment StartX=-2.77179 StartY=-200.304 StartZ=0 EndX=5.22821 EndY=-200.304 EndZ=0
    g1: LineSegment StartX=5.22821 StartY=-200.304 StartZ=0 EndX=5.22821 EndY=-197.304 EndZ=0
    g2: LineSegment StartX=-2.77179 StartY=-200.304 StartZ=0 EndX=-2.77179 EndY=-197.304 EndZ=0
    g3: LineSegment StartX=5.22821 StartY=-197.304 StartZ=0 EndX=8.22821 EndY=-197.304 EndZ=0
    g4: LineSegment StartX=-2.77179 StartY=-197.304 StartZ=0 EndX=-5.77179 EndY=-197.304 EndZ=0
    g5: LineSegment StartX=19.2282 StartY=-203.304 StartZ=0 EndX=19.2282 EndY=-206.304 EndZ=0
    g6: LineSegment StartX=-16.7718 StartY=-203.304 StartZ=0 EndX=-16.7718 EndY=-206.304 EndZ=0
    g7: LineSegment StartX=-16.7718 StartY=-206.304 StartZ=0 EndX=19.2282 EndY=-206.304 EndZ=0
    g8: Circle CenterX=-16.7718 CenterY=-203.304 CenterZ=0 NormalX=0 NormalY=0 NormalZ=1 AngleXU=0 Radius=1
    g9: Circle CenterX=-5.77179 CenterY=-203.304 CenterZ=0 NormalX=0 NormalY=0 NormalZ=1 AngleXU=0 Radius=1
    g10: Circle CenterX=-5.77179 CenterY=-197.304 CenterZ=0 NormalX=0 NormalY=0 NormalZ=1 AngleXU=0 Radius=1
    g11: BSplineCurve PolesCount=3 KnotsCount=2 Degree=2 IsPeriodic=0
    g12: GeomPoint X=-16.7718 Y=-203.304 Z=0
    g13: GeomPoint X=-5.77179 Y=-197.304 Z=0
    g14: Circle CenterX=19.2282 CenterY=-203.304 CenterZ=0 NormalX=0 NormalY=0 NormalZ=1 AngleXU=0 Radius=1
    g15: Circle CenterX=8.22821 CenterY=-203.304 CenterZ=0 NormalX=0 NormalY=0 NormalZ=1 AngleXU=0 Radius=1
    g16: Circle CenterX=8.22821 CenterY=-197.304 CenterZ=0 NormalX=0 NormalY=0 NormalZ=1 AngleXU=0 Radius=1
    g17: BSplineCurve PolesCount=3 KnotsCount=2 Degree=2 IsPeriodic=0
    g18: GeomPoint X=19.2282 Y=-203.304 Z=0
    g19: GeomPoint X=8.22821 Y=-197.304 Z=0
  constraints (41):
    c: Horizontal(g0)
    c: Distance(g0) = 8
    c: Coincident(g1,g0)
    c: Vertical(g1)
    c: Distance(g1) = 3
    c: Coincident(g2,g0)
    c: Vertical(g2)
    c: Distance(g2) = 3
    c: Coincident(g3,g1)
    c: Horizontal(g3)
    c: Distance(g3) = 3
    c: Coincident(g4,g2)
    c: Horizontal(g4)
    c: Distance(g4) = 3
    c: Vertical(g5)
    c: Vertical(g6)
    c: Coincident(g7,g6)
    c: Coincident(g7,g5)
    c: Weight(g8) = 1
    c: Equal(g8,g9)
    c: Equal(g8,g10)
    c: Coincident(g11,g4)
    c: InternalAlignment(g8,g11)
    c: InternalAlignment(g9,g11)
    c: InternalAlignment(g10,g11)
    c: InternalAlignment(g12,g11)
    c: InternalAlignment(g13,g11)
    c: Coincident(g17,g5)
    c: Weight(g14) = 1
    c: Equal(g14,g15)
    c: Equal(g14,g16)
    c: Coincident(g17,g3)
    c: InternalAlignment(g14,g17)
    c: InternalAlignment(g15,g17)
    c: InternalAlignment(g16,g17)
    c: InternalAlignment(g18,g17)
    c: InternalAlignment(g19,g17)
    c: Block(g7)
    c: Block(g17)
    c: Block(g11)
    c: Block(g6)
FEATURE [Part::Extrusion] Extrude003
  Base = -> Sketch002
  Dir = (0,0,1)
  DirMode = 2
  FaceMakerClass = Part::FaceMakerBullseye
  LengthFwd = 260
  LengthRev = 0
  Solid = true
  Symmetric = false
FEATURE [Part::Extrusion] Extrude
  Base = -> Sketch
  Dir = (0,0,1)
  DirMode = 2
  FaceMakerClass = Part::FaceMakerBullseye
  LengthFwd = 14
  LengthRev = 0
  Solid = true
  Symmetric = false
